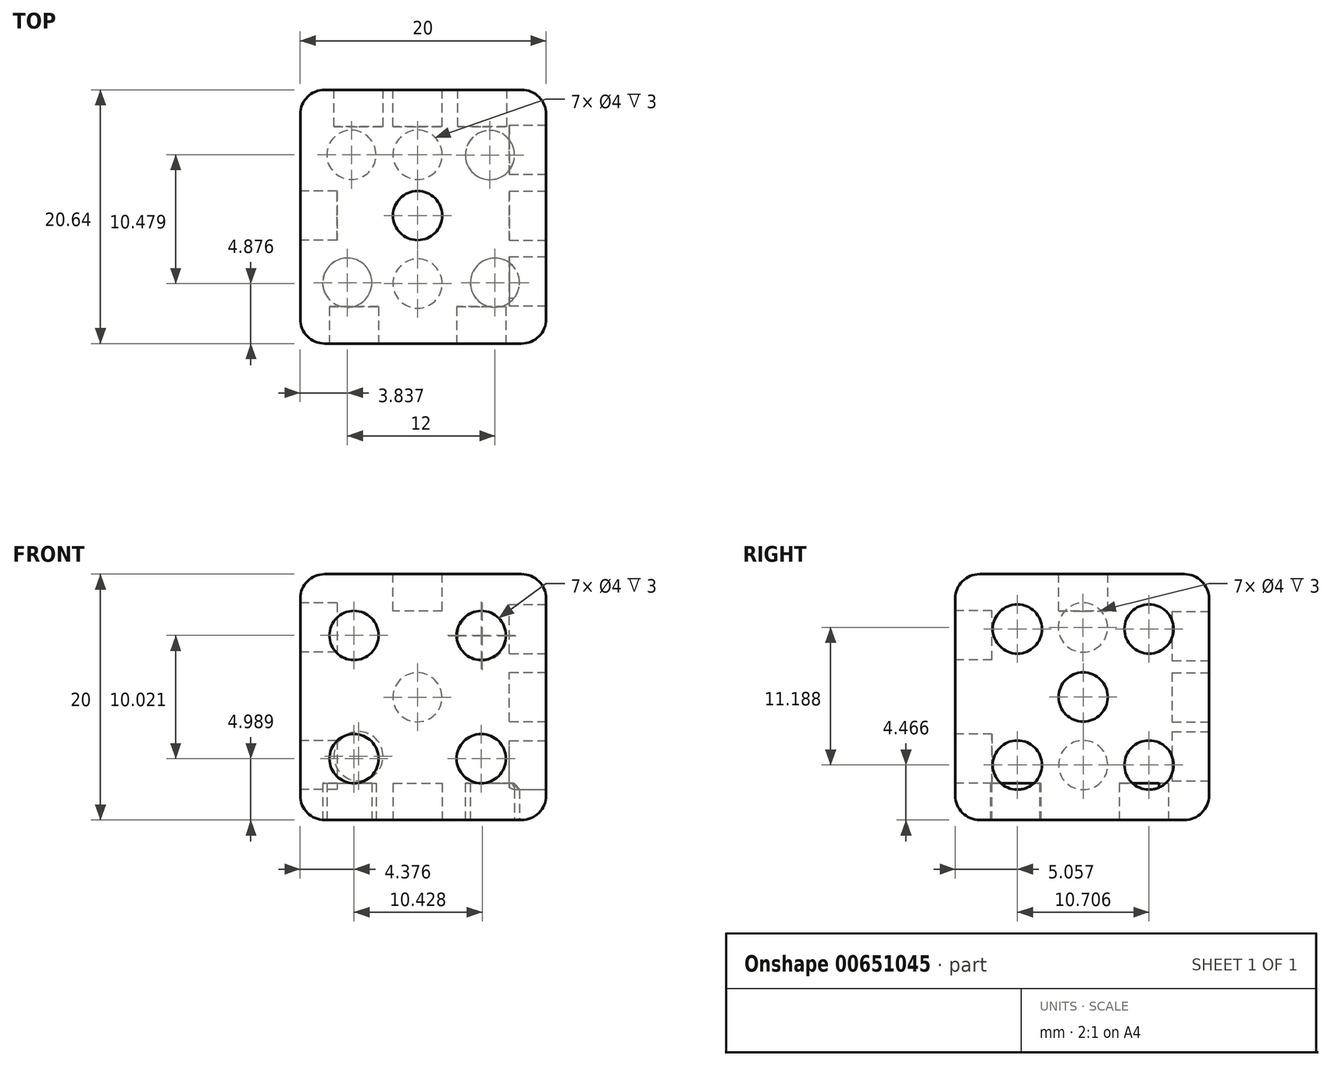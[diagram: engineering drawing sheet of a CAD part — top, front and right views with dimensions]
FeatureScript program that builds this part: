
annotation { "Feature Type Name" : "Feature", "Feature Type Description" : "" }
export const myFeature = defineFeature(function(context is Context, id is Id, definition is map)
    precondition{}
    {
        {
            var Q0;
            Q0=qCreatedBy(makeId("Top.planeOp"),FACE);
            var sketch = newSketch(context, id + "F0", { "sketchPlane" : qUnion([Q0])});
            skLineSegment(sketch, "E0.bottom", {"start": v(-9.55, 10.23) * mm, "end": v(10.45, 10.23) * mm});
            skLineSegment(sketch, "E0.top", {"start": v(-9.55, -10.4) * mm, "end": v(10.45, -10.4) * mm});
            skLineSegment(sketch, "E0.left", {"start": v(-9.55, 10.23) * mm, "end": v(-9.55, -10.4) * mm});
            skLineSegment(sketch, "E0.right", {"start": v(10.45, 10.23) * mm, "end": v(10.45, -10.4) * mm});
            skSolve(sketch);
        }
        {
            var Q0;
            Q0=makeQuery(id+"F0.imprint","IMPRINT",FACE,{"disambiguationData":[TD([[makeQuery(id+"F0.imprint","IMPRINT",EDGE,{"derivedFrom":sQuery(id+"F0.wireOp",EDGE,"E0.bottom")}),-1.0]])]});
            extrude(context, id + "F1", {"entities" : qUnion([Q0]), "endBound" : BoundingType.SYMMETRIC, "depth" : 20 * mm, "offsetDistance" : 25 * mm});
        }
        {
            var Q0;
            Q0=makeQuery(id+"F1.opExtrude","CAP_FACE",FACE,{"disambiguationData":[OSD([sQuery(id+"F0.wireOp",EDGE,"E0.bottom"),sQuery(id+"F0.wireOp",EDGE,"E0.top"),sQuery(id+"F0.wireOp",EDGE,"E0.left"),sQuery(id+"F0.wireOp",EDGE,"E0.right")])],"isStart":false});
            var sketch = newSketch(context, id + "F2", { "sketchPlane" : qUnion([Q0])});
            skCircle(sketch, "E1", {"center": v(0, 0) * mm, "radius": 2 * mm});
            skSolve(sketch);
        }
        {
            var Q0;
            Q0 = qSketchRegion(id + "F2", true);
            extrude(context, id + "F3", {"entities" : qUnion([Q0]), "operationType" : NewBodyOperationType.REMOVE, "oppositeDirection" : true, "depth" : 3 * mm, "offsetDistance" : 25 * mm});
        }
        {
            var Q0;
            Q0=makeQuery(id+"F1.opExtrude","CAP_FACE",FACE,{"disambiguationData":[OSD([sQuery(id+"F0.wireOp",EDGE,"E0.bottom"),sQuery(id+"F0.wireOp",EDGE,"E0.top"),sQuery(id+"F0.wireOp",EDGE,"E0.left"),sQuery(id+"F0.wireOp",EDGE,"E0.right")])],"isStart":true});
            var sketch = newSketch(context, id + "F4", { "sketchPlane" : qUnion([Q0])});
            skCircle(sketch, "E2", {"center": v(-5.71, 5.46) * mm, "radius": 2 * mm});
            skCircle(sketch, "E3.1.0.0", {"center": v(0, 5.53) * mm, "radius": 2 * mm});
            skCircle(sketch, "E3.2.0.0", {"center": v(6.29, 5.46) * mm, "radius": 2 * mm});
            skCircle(sketch, "E4", {"center": v(-5.39, -4.94) * mm, "radius": 2 * mm});
            skCircle(sketch, "E5", {"center": v(0, -4.94) * mm, "radius": 2 * mm});
            skCircle(sketch, "E6", {"center": v(5.88, -4.92) * mm, "radius": 2 * mm});
            skSolve(sketch);
        }
        {
            var Q0;
            Q0 = qSketchRegion(id + "F4", true);
            extrude(context, id + "F5", {"entities" : qUnion([Q0]), "operationType" : NewBodyOperationType.REMOVE, "oppositeDirection" : true, "depth" : 3 * mm, "offsetDistance" : 25 * mm});
        }
        {
            var Q0;
            Q0=makeQuery(id+"F1.opExtrude","SWEPT_FACE",FACE,{"disambiguationData":[OSD([sQuery(id+"F0.wireOp",EDGE,"E0.left")])]});
            var sketch = newSketch(context, id + "F6", { "sketchPlane" : qUnion([Q0])});
            skCircle(sketch, "E7", {"center": v(0.02, 5.65) * mm, "radius": 2 * mm});
            skCircle(sketch, "E8", {"center": v(0, -5.53) * mm, "radius": 2 * mm});
            skSolve(sketch);
        }
        {
            var Q0;
            Q0 = qSketchRegion(id + "F6", true);
            extrude(context, id + "F7", {"entities" : qUnion([Q0]), "operationType" : NewBodyOperationType.REMOVE, "oppositeDirection" : true, "depth" : 3 * mm, "offsetDistance" : 25 * mm});
        }
        {
            var Q0;
            Q0=makeQuery(id+"F1.opExtrude","SWEPT_FACE",FACE,{"disambiguationData":[OSD([sQuery(id+"F0.wireOp",EDGE,"E0.right")])]});
            var sketch = newSketch(context, id + "F8", { "sketchPlane" : qUnion([Q0])});
            skCircle(sketch, "E9", {"center": v(0, 0) * mm, "radius": 2 * mm});
            skCircle(sketch, "E10", {"center": v(-5.35, 5.53) * mm, "radius": 2 * mm});
            skCircle(sketch, "E11.MirrorC", {"center": v(5.35, 5.53) * mm, "radius": 2 * mm});
            skCircle(sketch, "E12.MirrorC", {"center": v(-5.35, -5.53) * mm, "radius": 2 * mm});
            skCircle(sketch, "E13.MirrorC", {"center": v(5.35, -5.53) * mm, "radius": 2 * mm});
            skSolve(sketch);
        }
        {
            var Q0;
            Q0 = qSketchRegion(id + "F8", true);
            extrude(context, id + "F9", {"entities" : qUnion([Q0]), "operationType" : NewBodyOperationType.REMOVE, "oppositeDirection" : true, "depth" : 3 * mm, "offsetDistance" : 25 * mm});
        }
        {
            var Q0;
            Q0=makeQuery(id+"F1.opExtrude","SWEPT_FACE",FACE,{"disambiguationData":[OSD([sQuery(id+"F0.wireOp",EDGE,"E0.bottom")])]});
            var sketch = newSketch(context, id + "F10", { "sketchPlane" : qUnion([Q0])});
            skCircle(sketch, "E14", {"center": v(0.01, -0.02) * mm, "radius": 2 * mm});
            skCircle(sketch, "E15", {"center": v(4.8, -4.8) * mm, "radius": 2 * mm});
            skCircle(sketch, "E16", {"center": v(-5.25, 4.96) * mm, "radius": 2 * mm});
            skSolve(sketch);
        }
        {
            var Q0;
            Q0 = qSketchRegion(id + "F10", true);
            extrude(context, id + "F11", {"entities" : qUnion([Q0]), "operationType" : NewBodyOperationType.REMOVE, "oppositeDirection" : true, "depth" : 3 * mm, "offsetDistance" : 25 * mm});
        }
        {
            var Q0;
            Q0=makeQuery(id+"F1.opExtrude","SWEPT_FACE",FACE,{"disambiguationData":[OSD([sQuery(id+"F0.wireOp",EDGE,"E0.top")])]});
            var sketch = newSketch(context, id + "F12", { "sketchPlane" : qUnion([Q0])});
            skCircle(sketch, "E17", {"center": v(5.17, 5.01) * mm, "radius": 2 * mm});
            skCircle(sketch, "E18.MirrorC", {"center": v(-5.17, 5.01) * mm, "radius": 2 * mm});
            skCircle(sketch, "E19.MirrorC", {"center": v(-5.17, -5.01) * mm, "radius": 2 * mm});
            skCircle(sketch, "E20.MirrorC", {"center": v(5.17, -5.01) * mm, "radius": 2 * mm});
            skSolve(sketch);
        }
        {
            var Q0;
            Q0 = qSketchRegion(id + "F12", true);
            extrude(context, id + "F13", {"entities" : qUnion([Q0]), "operationType" : NewBodyOperationType.REMOVE, "oppositeDirection" : true, "depth" : 3 * mm, "offsetDistance" : 25 * mm});
        }
        {
            var Q0;
            Q0=makeQuery(id+"F1.opExtrude","SWEPT_EDGE",EDGE,{"disambiguationData":[OSD([sQuery(id+"F0.wireOp",EDGE,"E0.top"),sQuery(id+"F0.wireOp",EDGE,"E0.right")])]});
            var Q1;
            Q1=makeQuery(id+"F1.opExtrude","CAP_EDGE",EDGE,{"disambiguationData":[OSD([sQuery(id+"F0.wireOp",EDGE,"E0.top")])],"isStart":false});
            var Q2;
            Q2=makeQuery(id+"F1.opExtrude","SWEPT_EDGE",EDGE,{"disambiguationData":[OSD([sQuery(id+"F0.wireOp",EDGE,"E0.top"),sQuery(id+"F0.wireOp",EDGE,"E0.left")])]});
            var Q3;
            Q3=makeQuery(id+"F1.opExtrude","CAP_EDGE",EDGE,{"disambiguationData":[OSD([sQuery(id+"F0.wireOp",EDGE,"E0.left")])],"isStart":false});
            var Q4;
            Q4=makeQuery(id+"F1.opExtrude","SWEPT_EDGE",EDGE,{"disambiguationData":[OSD([sQuery(id+"F0.wireOp",EDGE,"E0.bottom"),sQuery(id+"F0.wireOp",EDGE,"E0.left")])]});
            var Q5;
            Q5=makeQuery(id+"F1.opExtrude","CAP_EDGE",EDGE,{"disambiguationData":[OSD([sQuery(id+"F0.wireOp",EDGE,"E0.left")])],"isStart":true});
            var Q6;
            Q6=makeQuery(id+"F1.opExtrude","CAP_EDGE",EDGE,{"disambiguationData":[OSD([sQuery(id+"F0.wireOp",EDGE,"E0.top")])],"isStart":true});
            var Q7;
            Q7=makeQuery(id+"F1.opExtrude","CAP_EDGE",EDGE,{"disambiguationData":[OSD([sQuery(id+"F0.wireOp",EDGE,"E0.right")])],"isStart":true});
            var Q8;
            Q8=makeQuery(id+"F1.opExtrude","CAP_EDGE",EDGE,{"disambiguationData":[OSD([sQuery(id+"F0.wireOp",EDGE,"E0.bottom")])],"isStart":true});
            var Q9;
            Q9=makeQuery(id+"F1.opExtrude","SWEPT_EDGE",EDGE,{"disambiguationData":[OSD([sQuery(id+"F0.wireOp",EDGE,"E0.bottom"),sQuery(id+"F0.wireOp",EDGE,"E0.right")])]});
            var Q10;
            Q10=makeQuery(id+"F1.opExtrude","CAP_EDGE",EDGE,{"disambiguationData":[OSD([sQuery(id+"F0.wireOp",EDGE,"E0.bottom")])],"isStart":false});
            var Q11;
            Q11=makeQuery(id+"F1.opExtrude","CAP_EDGE",EDGE,{"disambiguationData":[OSD([sQuery(id+"F0.wireOp",EDGE,"E0.right")])],"isStart":false});
            fillet(context, id + "F14", {"entities" : qUnion([Q0, Q1, Q2, Q3, Q4, Q5, Q6, Q7, Q8, Q9, Q10, Q11]), "radius" : 2 * mm, "tangentPropagation" : true, "allowEdgeOverflow" : false});
        }
    });
